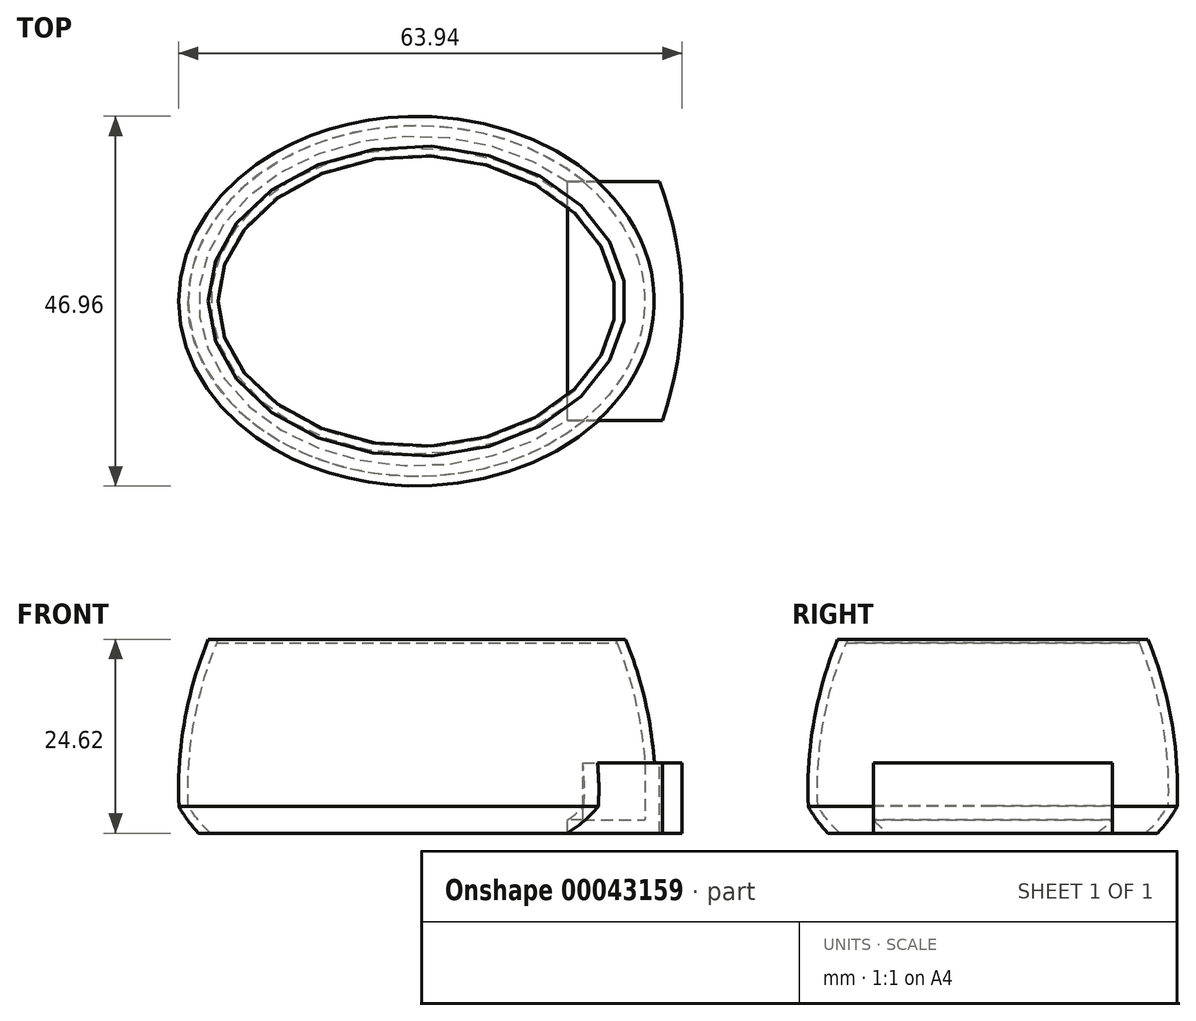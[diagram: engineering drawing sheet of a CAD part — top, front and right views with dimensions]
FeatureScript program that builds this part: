
annotation { "Feature Type Name" : "Feature", "Feature Type Description" : "" }
export const myFeature = defineFeature(function(context is Context, id is Id, definition is map)
    precondition{}
    {
        {
            var Q0;
            Q0=qCreatedBy(makeId("Top.planeOp"),FACE);
            var sketch = newSketch(context, id + "F0", { "sketchPlane" : qUnion([Q0])});
            skEllipse(sketch, "E0", {"center": v(0, 0) * mm, "majorRadius": 30 * mm, "minorRadius": 23.2 * mm, "majorAxis": v(-1, 0)});
            skSolve(sketch);
        }
        {
            var Q0;
            Q0=qCreatedBy(makeId("Front.planeOp"),FACE);
            var sketch = newSketch(context, id + "F1", { "sketchPlane" : qUnion([Q0])});
            skArc(sketch, "E1", {"start": v(-26.5, 21.21) * mm, "mid": v(-29.52, 10.8) * mm, "end": v(-30.23, 0) * mm});
            skArc(sketch, "E2.0", {"start": v(-25.4, 20.76) * mm, "mid": v(-28.33, 10.6) * mm, "end": v(-29.03, 0.05) * mm});
            skLineSegment(sketch, "E3", {"start": v(-30.23, 0) * mm, "end": v(-29.03, 0) * mm});
            skLineSegment(sketch, "E4", {"start": v(-29.03, 0) * mm, "end": v(-29.03, 0.05) * mm});
            skLineSegment(sketch, "E5", {"start": v(-26.5, 21.21) * mm, "end": v(-25.24, 21.21) * mm});
            skLineSegment(sketch, "E6", {"start": v(-25.24, 21.21) * mm, "end": v(-25.4, 20.76) * mm});
            skArc(sketch, "E7", {"start": v(-30.23, 0) * mm, "mid": v(-29.1, -1.79) * mm, "end": v(-27.73, -3.4) * mm});
            skArc(sketch, "E8", {"start": v(-29.03, 0.05) * mm, "mid": v(-27.75, -1.78) * mm, "end": v(-26.21, -3.4) * mm});
            skLineSegment(sketch, "E9", {"start": v(-27.73, -3.4) * mm, "end": v(-26.21, -3.4) * mm});
            skLineSegment(sketch, "E10", {"start": v(34.03, 5.55) * mm, "end": v(34.03, -3.8) * mm});
            skLineSegment(sketch, "E11", {"start": v(34.03, 5.55) * mm, "end": v(19.16, 5.55) * mm});
            skLineSegment(sketch, "E12", {"start": v(19.16, 5.55) * mm, "end": v(19.16, -3.8) * mm});
            skLineSegment(sketch, "E13", {"start": v(19.16, -3.8) * mm, "end": v(34.03, -3.8) * mm});
            skSolve(sketch);
        }
        {
            var Q0;
            Q0=makeQuery(id+"F1.imprint","IMPRINT",FACE,{"disambiguationData":[TD([[makeQuery(id+"F1.imprint","IMPRINT",EDGE,{"derivedFrom":sQuery(id+"F1.wireOp",EDGE,"E1")}),1.0]])]});
            var Q1;
            Q1=sQuery(id+"F0.wireOp",EDGE,"E0");
            sweep(context, id + "F2", {"profiles" : qUnion([Q0]), "path" : qUnion([Q1])});
        }
        {
            var Q0;
            Q0=makeQuery(id+"F1.imprint","IMPRINT",FACE,{"disambiguationData":[TD([[makeQuery(id+"F1.imprint","IMPRINT",EDGE,{"derivedFrom":sQuery(id+"F1.wireOp",EDGE,"E3")}),-1.0]])]});
            var Q1;
            Q1=sQuery(id+"F0.wireOp",EDGE,"E0");
            sweep(context, id + "F3", {"operationType" : NewBodyOperationType.ADD, "profiles" : qUnion([Q0]), "path" : qUnion([Q1])});
        }
        {
            var Q0;
            Q0=makeQuery(id+"F1.imprint","IMPRINT",FACE,{"disambiguationData":[TD([[makeQuery(id+"F1.imprint","IMPRINT",EDGE,{"derivedFrom":sQuery(id+"F1.wireOp",EDGE,"E10")}),-1.0]])]});
            extrude(context, id + "F4", {"entities" : qUnion([Q0]), "operationType" : NewBodyOperationType.ADD, "endBound" : BoundingType.SYMMETRIC, "depth" : 30.34 * mm});
        }
        {
            var Q0;
            {var subQ0=sQuery(id+"F1.wireOp",EDGE,"E11");var subQ1=sQuery(id+"F1.wireOp",EDGE,"E10");Q0=makeQuery(id+"F4.boolean.opBoolean","SPLIT",FACE,{"disambiguationData":[TD([makeQuery(id+"F4.opExtrude","SWEPT_FACE",FACE,{"disambiguationData":[OSD([subQ1])]})])],"derivedFrom":makeQuery(id+"F4.opExtrude","SWEPT_FACE",FACE,{"disambiguationData":[OSD([subQ0])]})});}
            var sketch = newSketch(context, id + "F5", { "sketchPlane" : qUnion([Q0])});
            skArc(sketch, "E14", {"start": v(31.16, -15.17) * mm, "mid": v(33.66, 0.03) * mm, "end": v(30.83, 15.17) * mm});
            skLineSegment(sketch, "E15", {"start": v(30.83, 15.17) * mm, "end": v(34.03, 15.17) * mm});
            skLineSegment(sketch, "E16", {"start": v(34.03, 15.17) * mm, "end": v(34.03, -15.17) * mm});
            skLineSegment(sketch, "E17", {"start": v(34.03, -15.17) * mm, "end": v(31.16, -15.17) * mm});
            skSolve(sketch);
        }
        {
            var Q0;
            Q0=makeQuery(id+"F5.imprint","IMPRINT",FACE,{"disambiguationData":[TD([[makeQuery(id+"F5.imprint","IMPRINT",EDGE,{"derivedFrom":sQuery(id+"F5.wireOp",EDGE,"E14")}),-1.0]])]});
            extrude(context, id + "F6", {"entities" : qUnion([Q0]), "operationType" : NewBodyOperationType.REMOVE, "endBound" : BoundingType.THROUGH_ALL, "oppositeDirection" : true, "depth" : 25 * mm});
        }
        {
            var Q0;
            Q0=makeQuery(id+"F4.opExtrude","SWEPT_FACE",FACE,{"disambiguationData":[OSD([sQuery(id+"F1.wireOp",EDGE,"E13")])]});
            var Q1;
            Q1=makeQuery(id+"F3.opSweep","SWEPT_FACE",FACE,{"disambiguationData":[OSD([sQuery(id+"F0.wireOp",EDGE,"E0"),sQuery(id+"F1.wireOp",EDGE,"E9")])]});
            extrude(context, id + "F7", {"entities" : qUnion([Q0]), "operationType" : NewBodyOperationType.REMOVE, "endBound" : BoundingType.UP_TO_SURFACE, "oppositeDirection" : true, "endBoundEntityFace" : qUnion([Q1]), "depth" : 25 * mm});
        }
        {
            var Q0;
            {var subQ0=sQuery(id+"F1.wireOp",EDGE,"E11");var subQ2=sQuery(id+"F1.wireOp",EDGE,"E12");Q0=makeQuery(id+"F4.boolean.opBoolean","SPLIT",FACE,{"disambiguationData":[TD([makeQuery(id+"F4.opExtrude","SWEPT_FACE",FACE,{"disambiguationData":[OSD([subQ2])]})])],"derivedFrom":makeQuery(id+"F4.opExtrude","SWEPT_FACE",FACE,{"disambiguationData":[OSD([subQ0])]})});}
            extrude(context, id + "F8", {"entities" : qUnion([Q0]), "operationType" : NewBodyOperationType.REMOVE, "oppositeDirection" : true, "depth" : 7.28 * mm});
        }
    });
